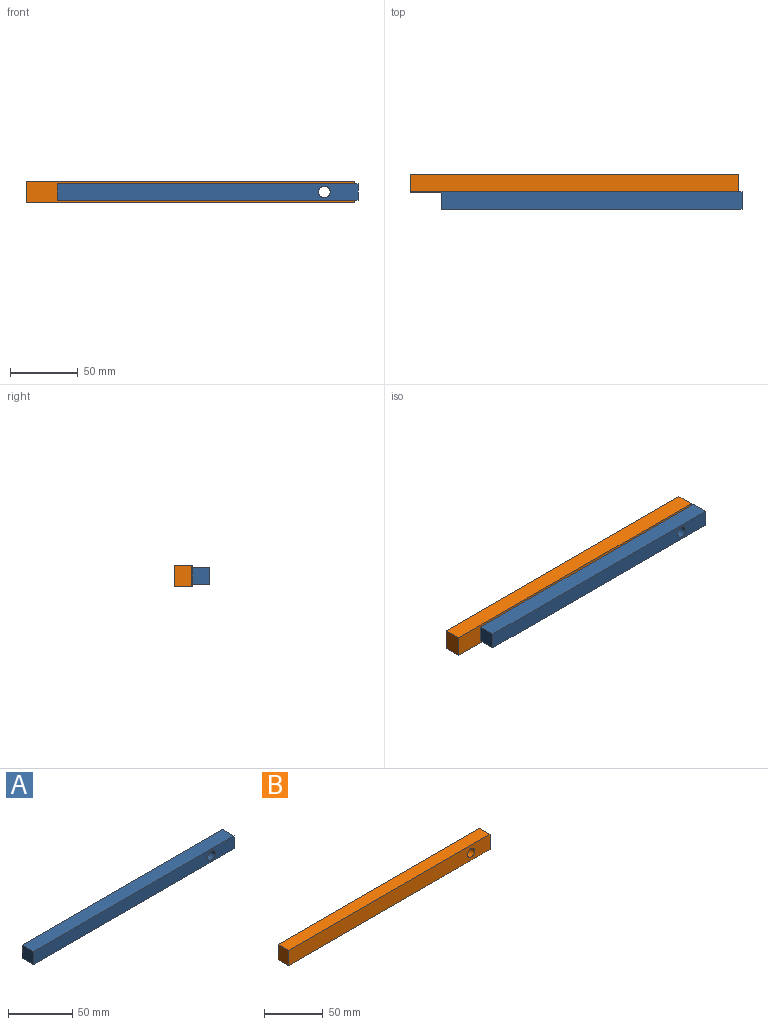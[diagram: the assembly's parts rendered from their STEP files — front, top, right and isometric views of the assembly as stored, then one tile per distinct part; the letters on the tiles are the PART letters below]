
ASSEMBLY  parts=2 mates=1
PART A: 7 faces, bbox 221.3x12.7x12.4 mm
  f0: plane 12.7x12.38mm, normal (1,0,0), area 157.2mm2, adj f1,f3,f5,f6
  f1: plane 221.32x12.7mm, normal (0,0,1), area 2810.8mm2, adj f0,f2,f5,f6
  f2: plane 12.7x12.38mm, normal (-1,0,0), area 157.2mm2, adj f1,f3,f5,f6
  f3: plane 221.32x12.7mm, normal (0,0,-1), area 2810.8mm2, adj f0,f2,f5,f6
  f4: cylinder r=4.27mm len=12.7mm, axis (0,1,0), area 340.8mm2, adj f5,f6
  f5: plane 221.32x12.38mm, normal (0,-1,0), area 2681.7mm2, adj f0,f1,f2,f3,f4
  f6: plane 221.32x12.38mm, normal (0,1,0), area 2681.7mm2, adj f0,f1,f2,f3,f4
PART B: 7 faces, bbox 242x12.7x15.8 mm
  f0: plane 242.04x12.7mm, normal (0,0,-1), area 3074mm2, adj f1,f4,f5,f6
  f1: plane 15.83x12.7mm, normal (1,0,0), area 201mm2, adj f0,f2,f5,f6
  f2: plane 242.04x12.7mm, normal (0,0,1), area 3074mm2, adj f1,f4,f5,f6
  f3: cylinder r=4.33mm len=12.7mm, axis (0,1,0), area 345.4mm2, adj f5,f6
  f4: plane 15.83x12.7mm, normal (-1,0,0), area 201mm2, adj f0,f2,f5,f6
  f5: plane 242.04x15.83mm, normal (0,-1,0), area 3772.5mm2, adj f0,f1,f2,f3,f4
  f6: plane 242.04x15.83mm, normal (0,1,0), area 3772.5mm2, adj f0,f1,f2,f3,f4
PLACE A rot(axis=(1,0,0),180deg) t=(-4.2,-23.42,8.05)mm
PLACE B t=(-16.87,1.98,8.05)mm fixed
MATE revolute A.f4 <-> B.f3  axis (0,1,0) through (81.71,-10.72,8.05)mm
